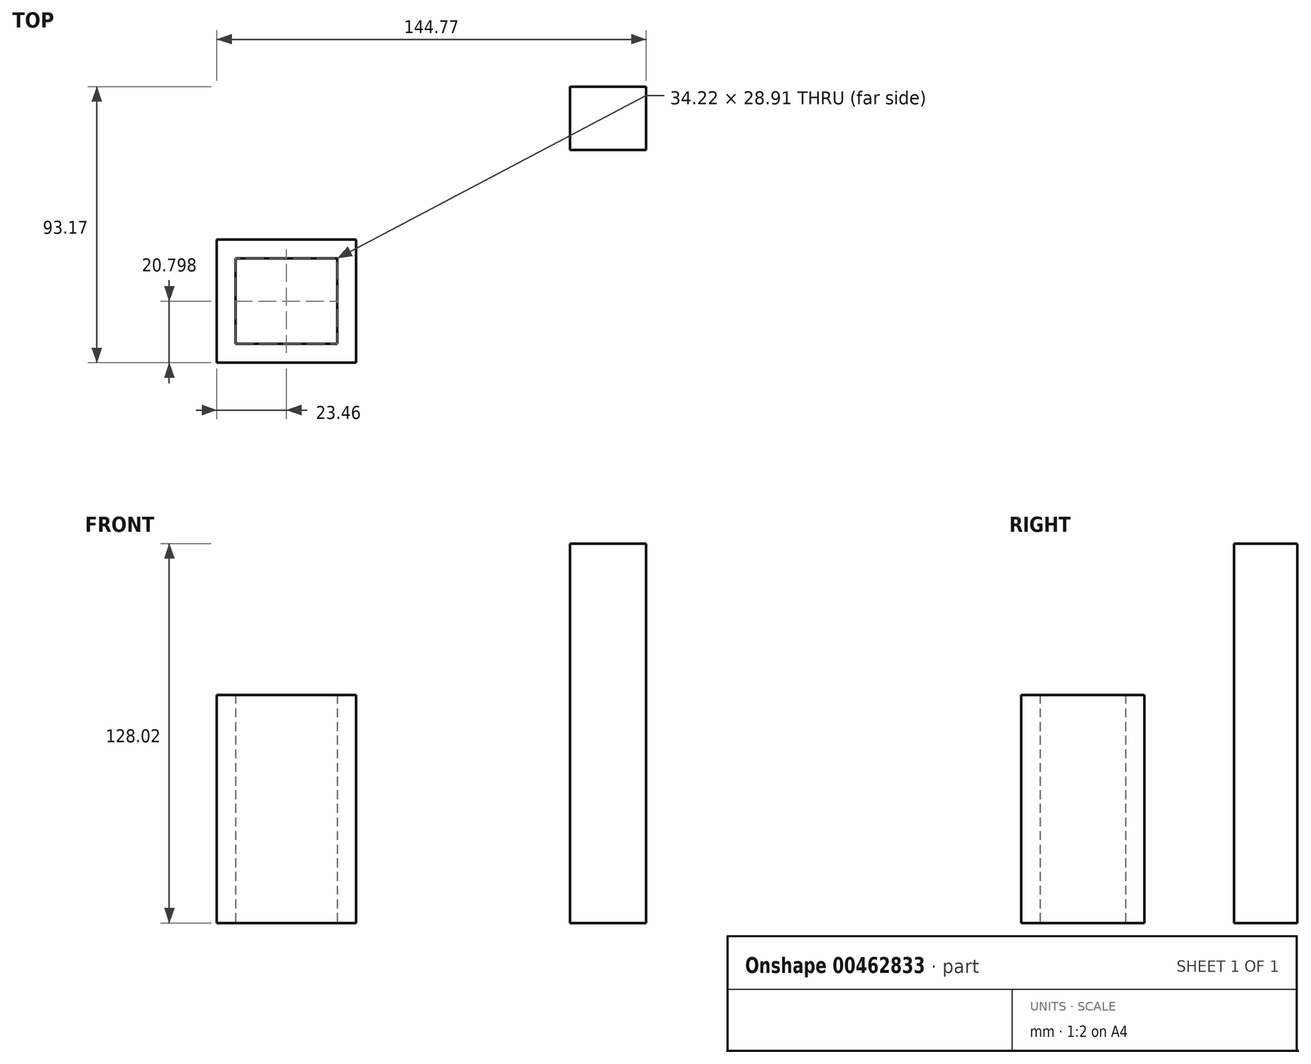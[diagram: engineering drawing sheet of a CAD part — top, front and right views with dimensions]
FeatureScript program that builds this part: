
annotation { "Feature Type Name" : "Feature", "Feature Type Description" : "" }
export const myFeature = defineFeature(function(context is Context, id is Id, definition is map)
    precondition{}
    {
        {
            var Q0;
            Q0=qCreatedBy(makeId("Top.planeOp"),FACE);
            var sketch = newSketch(context, id + "F0", { "sketchPlane" : qUnion([Q0])});
            skLineSegment(sketch, "E0.bottom", {"start": v(-40.94, -57.98) * mm, "end": v(-87.86, -57.98) * mm});
            skLineSegment(sketch, "E0.top", {"start": v(-40.94, -16.38) * mm, "end": v(-87.86, -16.38) * mm});
            skLineSegment(sketch, "E0.left", {"start": v(-40.94, -57.98) * mm, "end": v(-40.94, -16.38) * mm});
            skLineSegment(sketch, "E0.right", {"start": v(-87.86, -57.98) * mm, "end": v(-87.86, -16.38) * mm});
            skLineSegment(sketch, "E1.0", {"start": v(-47.3, -51.63) * mm, "end": v(-81.5, -51.63) * mm});
            skLineSegment(sketch, "E1.1", {"start": v(-47.3, -51.63) * mm, "end": v(-47.3, -22.73) * mm});
            skLineSegment(sketch, "E1.2", {"start": v(-47.3, -22.73) * mm, "end": v(-81.5, -22.73) * mm});
            skLineSegment(sketch, "E1.3", {"start": v(-81.5, -51.63) * mm, "end": v(-81.5, -22.73) * mm});
            skSolve(sketch);
        }
        {
            var Q0;
            Q0=makeQuery(id+"F0.imprint","IMPRINT",FACE,{"disambiguationData":[TD([[makeQuery(id+"F0.imprint","IMPRINT",EDGE,{"derivedFrom":sQuery(id+"F0.wireOp",EDGE,"E0.bottom")}),-1.0]])]});
            extrude(context, id + "F1", {"entities" : qUnion([Q0]), "depth" : 76.96 * mm});
        }
        {
            var Q0;
            Q0=qCreatedBy(makeId("Top.planeOp"),FACE);
            var sketch = newSketch(context, id + "F2", { "sketchPlane" : qUnion([Q0])});
            skLineSegment(sketch, "E2.bottom", {"start": v(56.9, 13.78) * mm, "end": v(31.2, 13.78) * mm});
            skLineSegment(sketch, "E2.top", {"start": v(56.9, 35.19) * mm, "end": v(31.2, 35.19) * mm});
            skLineSegment(sketch, "E2.left", {"start": v(56.9, 13.78) * mm, "end": v(56.9, 35.19) * mm});
            skLineSegment(sketch, "E2.right", {"start": v(31.2, 13.78) * mm, "end": v(31.2, 35.19) * mm});
            skSolve(sketch);
        }
        {
            var Q0;
            Q0=makeQuery(id+"F2.imprint","IMPRINT",FACE,{"disambiguationData":[TD([[makeQuery(id+"F2.imprint","IMPRINT",EDGE,{"derivedFrom":sQuery(id+"F2.wireOp",EDGE,"E2.bottom")}),-1.0]])]});
            extrude(context, id + "F3", {"entities" : qUnion([Q0]), "depth" : 128.02 * mm});
        }
    });
